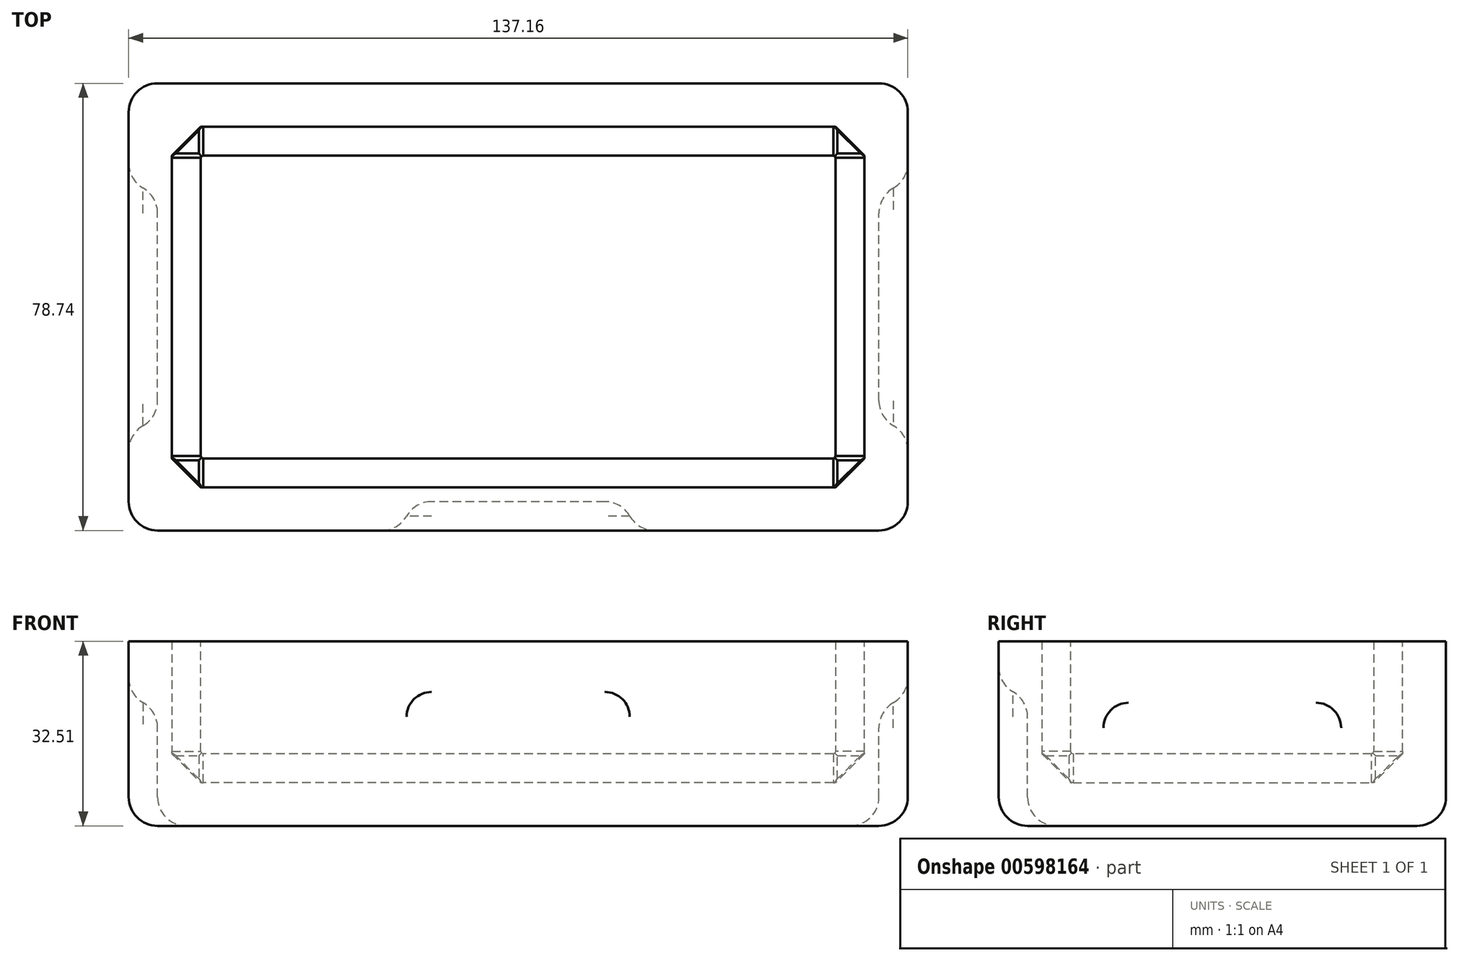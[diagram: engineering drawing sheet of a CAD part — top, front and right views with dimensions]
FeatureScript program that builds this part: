
annotation { "Feature Type Name" : "Feature", "Feature Type Description" : "" }
export const myFeature = defineFeature(function(context is Context, id is Id, definition is map)
    precondition{}
    {
        {
            var Q0;
            Q0=qCreatedBy(makeId("Top.planeOp"),FACE);
            var sketch = newSketch(context, id + "F0", { "sketchPlane" : qUnion([Q0])});
            skLineSegment(sketch, "E0.bottom", {"start": v(68.58, -39.37) * mm, "end": v(-68.58, -39.37) * mm});
            skLineSegment(sketch, "E0.top", {"start": v(68.58, 39.37) * mm, "end": v(-68.58, 39.37) * mm});
            skLineSegment(sketch, "E0.left", {"start": v(68.58, -39.37) * mm, "end": v(68.58, 39.37) * mm});
            skLineSegment(sketch, "E0.right", {"start": v(-68.58, -39.37) * mm, "end": v(-68.58, 39.37) * mm});
            skPoint(sketch, "E0.middle", {"position": v(0, 0) * mm});
            skSolve(sketch);
        }
        {
            var Q0;
            Q0 = qSketchRegion(id + "F0", true);
            extrude(context, id + "F1", {"entities" : qUnion([Q0]), "depth" : 32.5 * mm, "offsetDistance" : 25.4 * mm});
        }
        {
            var Q0;
            Q0=makeQuery(id+"F1.opExtrude","CAP_FACE",FACE,{"disambiguationData":[OSD([sQuery(id+"F0.wireOp",EDGE,"E0.bottom"),sQuery(id+"F0.wireOp",EDGE,"E0.top"),sQuery(id+"F0.wireOp",EDGE,"E0.left"),sQuery(id+"F0.wireOp",EDGE,"E0.right")])],"isStart":false});
            shell(context, id + "F2", {"entities" : qUnion([Q0]), "thickness" : 7.62 * mm});
        }
        {
            var Q0;
            Q0=makeQuery(id+"F2.opShell","OFFSET_EDGE",EDGE,{"disambiguationData":[OSD([sQuery(id+"F0.wireOp",EDGE,"E0.top"),sQuery(id+"F0.wireOp",EDGE,"E0.left")])]});
            var Q1;
            {var subQ0=sQuery(id+"F0.wireOp",EDGE,"E0.left");Q1=makeQuery(id+"F2.opShell","OFFSET_EDGE",EDGE,{"disambiguationData":[OSD([subQ0]),TDD([makeQuery(id+"F1.opExtrude","CAP_EDGE",EDGE,{"disambiguationData":[OSD([subQ0])],"isStart":true})])]});}
            var Q2;
            {var subQ0=sQuery(id+"F0.wireOp",EDGE,"E0.top");Q2=makeQuery(id+"F2.opShell","OFFSET_EDGE",EDGE,{"disambiguationData":[OSD([subQ0]),TDD([makeQuery(id+"F1.opExtrude","CAP_EDGE",EDGE,{"disambiguationData":[OSD([subQ0])],"isStart":true})])]});}
            var Q3;
            Q3=makeQuery(id+"F2.opShell","OFFSET_EDGE",EDGE,{"disambiguationData":[OSD([sQuery(id+"F0.wireOp",EDGE,"E0.top"),sQuery(id+"F0.wireOp",EDGE,"E0.right")])]});
            var Q4;
            {var subQ0=sQuery(id+"F0.wireOp",EDGE,"E0.right");Q4=makeQuery(id+"F2.opShell","OFFSET_EDGE",EDGE,{"disambiguationData":[OSD([subQ0]),TDD([makeQuery(id+"F1.opExtrude","CAP_EDGE",EDGE,{"disambiguationData":[OSD([subQ0])],"isStart":true})])]});}
            var Q5;
            {var subQ0=sQuery(id+"F0.wireOp",EDGE,"E0.bottom");Q5=makeQuery(id+"F2.opShell","OFFSET_EDGE",EDGE,{"disambiguationData":[OSD([subQ0]),TDD([makeQuery(id+"F1.opExtrude","CAP_EDGE",EDGE,{"disambiguationData":[OSD([subQ0])],"isStart":true})])]});}
            var Q6;
            Q6=makeQuery(id+"F2.opShell","OFFSET_EDGE",EDGE,{"disambiguationData":[OSD([sQuery(id+"F0.wireOp",EDGE,"E0.bottom"),sQuery(id+"F0.wireOp",EDGE,"E0.left")])]});
            var Q7;
            Q7=makeQuery(id+"F2.opShell","OFFSET_EDGE",EDGE,{"disambiguationData":[OSD([sQuery(id+"F0.wireOp",EDGE,"E0.bottom"),sQuery(id+"F0.wireOp",EDGE,"E0.right")])]});
            chamfer(context, id + "F3", {"entities" : qUnion([Q0, Q1, Q2, Q3, Q4, Q5, Q6, Q7]), "width" : 5.08 * mm, "tangentPropagation" : true});
        }
        {
            var Q0;
            Q0=makeQuery(id+"F1.opExtrude","SWEPT_FACE",FACE,{"disambiguationData":[OSD([sQuery(id+"F0.wireOp",EDGE,"E0.bottom")])]});
            var sketch = newSketch(context, id + "F4", { "sketchPlane" : qUnion([Q0])});
            skLineSegment(sketch, "E1.bottom", {"start": v(-20.32, 0) * mm, "end": v(20.32, 0) * mm});
            skLineSegment(sketch, "E1.top", {"start": v(-20.32, 24.27) * mm, "end": v(20.32, 24.27) * mm});
            skLineSegment(sketch, "E1.left", {"start": v(-20.32, 0) * mm, "end": v(-20.32, 24.27) * mm});
            skLineSegment(sketch, "E1.right", {"start": v(20.32, 0) * mm, "end": v(20.32, 24.27) * mm});
            skSolve(sketch);
        }
        {
            var Q0;
            Q0 = qSketchRegion(id + "F4", true);
            extrude(context, id + "F5", {"entities" : qUnion([Q0]), "operationType" : NewBodyOperationType.REMOVE, "oppositeDirection" : true, "depth" : 5.08 * mm, "offsetDistance" : 25.4 * mm});
        }
        {
            var Q0;
            Q0=makeQuery(id+"F1.opExtrude","SWEPT_FACE",FACE,{"disambiguationData":[OSD([sQuery(id+"F0.wireOp",EDGE,"E0.left")])]});
            var sketch = newSketch(context, id + "F6", { "sketchPlane" : qUnion([Q0])});
            skLineSegment(sketch, "E2.bottom", {"start": v(-21.6, 0) * mm, "end": v(21.59, 0) * mm});
            skLineSegment(sketch, "E2.top", {"start": v(-21.6, 22.35) * mm, "end": v(21.59, 22.35) * mm});
            skLineSegment(sketch, "E2.left", {"start": v(-21.6, 0) * mm, "end": v(-21.6, 22.35) * mm});
            skLineSegment(sketch, "E2.right", {"start": v(21.59, 0) * mm, "end": v(21.59, 22.35) * mm});
            skSolve(sketch);
        }
        {
            var Q0;
            Q0=makeQuery(id+"F6.imprint","IMPRINT",FACE,{"disambiguationData":[TD([[makeQuery(id+"F6.imprint","IMPRINT",EDGE,{"derivedFrom":sQuery(id+"F6.wireOp",EDGE,"E2.bottom")}),1.0]])]});
            extrude(context, id + "F7", {"entities" : qUnion([Q0]), "operationType" : NewBodyOperationType.REMOVE, "oppositeDirection" : true, "depth" : 5.08 * mm, "offsetDistance" : 25.4 * mm});
        }
        {
            var Q0;
            Q0=makeQuery(id+"F1.opExtrude","SWEPT_FACE",FACE,{"disambiguationData":[OSD([sQuery(id+"F0.wireOp",EDGE,"E0.right")])]});
            var sketch = newSketch(context, id + "F8", { "sketchPlane" : qUnion([Q0])});
            skLineSegment(sketch, "E3.bottom", {"start": v(-21.6, 0) * mm, "end": v(21.59, 0) * mm});
            skLineSegment(sketch, "E3.top", {"start": v(-21.6, 22.35) * mm, "end": v(21.59, 22.35) * mm});
            skLineSegment(sketch, "E3.left", {"start": v(-21.6, 0) * mm, "end": v(-21.6, 22.35) * mm});
            skLineSegment(sketch, "E3.right", {"start": v(21.59, 0) * mm, "end": v(21.59, 22.35) * mm});
            skSolve(sketch);
        }
        {
            var Q0;
            Q0 = qSketchRegion(id + "F8", true);
            extrude(context, id + "F9", {"entities" : qUnion([Q0]), "operationType" : NewBodyOperationType.REMOVE, "oppositeDirection" : true, "depth" : 5.08 * mm, "offsetDistance" : 25.4 * mm});
        }
        {
            var Q0;
            Q0=makeQuery(id+"F9.boolean.opBoolean","COPY",EDGE,{"derivedFrom":makeQuery(id+"F9.opExtrude","SWEPT_EDGE",EDGE,{"disambiguationData":[OSD([sQuery(id+"F8.wireOp",EDGE,"E3.top"),sQuery(id+"F8.wireOp",EDGE,"E3.left")])]})});
            var Q1;
            Q1=makeQuery(id+"F9.boolean.opBoolean","COPY",EDGE,{"derivedFrom":makeQuery(id+"F9.opExtrude","CAP_EDGE",EDGE,{"disambiguationData":[OSD([sQuery(id+"F8.wireOp",EDGE,"E3.top")])],"isStart":false})});
            var Q2;
            Q2=makeQuery(id+"F9.boolean.opBoolean","COPY",EDGE,{"derivedFrom":makeQuery(id+"F9.opExtrude","SWEPT_EDGE",EDGE,{"disambiguationData":[OSD([sQuery(id+"F8.wireOp",EDGE,"E3.top"),sQuery(id+"F8.wireOp",EDGE,"E3.right")])]})});
            var Q3;
            Q3=makeQuery(id+"F9.boolean.opBoolean","COPY",EDGE,{"derivedFrom":makeQuery(id+"F9.opExtrude","CAP_EDGE",EDGE,{"disambiguationData":[OSD([sQuery(id+"F8.wireOp",EDGE,"E3.left")])],"isStart":false})});
            var Q4;
            Q4=makeQuery(id+"F9.boolean.opBoolean","COPY",EDGE,{"derivedFrom":makeQuery(id+"F9.opExtrude","CAP_EDGE",EDGE,{"disambiguationData":[OSD([sQuery(id+"F8.wireOp",EDGE,"E3.right")])],"isStart":false})});
            fillet(context, id + "F10", {"entities" : qUnion([Q0, Q1, Q2, Q3, Q4]), "radius" : 5.08 * mm, "tangentPropagation" : true, "allowEdgeOverflow" : false});
        }
        {
            var Q0;
            Q0=makeQuery(id+"F5.boolean.opBoolean","COPY",EDGE,{"derivedFrom":makeQuery(id+"F5.opExtrude","SWEPT_EDGE",EDGE,{"disambiguationData":[OSD([sQuery(id+"F4.wireOp",EDGE,"E1.top"),sQuery(id+"F4.wireOp",EDGE,"E1.left")])]})});
            var Q1;
            Q1=makeQuery(id+"F5.boolean.opBoolean","COPY",EDGE,{"derivedFrom":makeQuery(id+"F5.opExtrude","CAP_EDGE",EDGE,{"disambiguationData":[OSD([sQuery(id+"F4.wireOp",EDGE,"E1.top")])],"isStart":false})});
            var Q2;
            Q2=makeQuery(id+"F5.boolean.opBoolean","COPY",EDGE,{"derivedFrom":makeQuery(id+"F5.opExtrude","SWEPT_EDGE",EDGE,{"disambiguationData":[OSD([sQuery(id+"F4.wireOp",EDGE,"E1.top"),sQuery(id+"F4.wireOp",EDGE,"E1.right")])]})});
            var Q3;
            Q3=makeQuery(id+"F5.boolean.opBoolean","COPY",EDGE,{"derivedFrom":makeQuery(id+"F5.opExtrude","CAP_EDGE",EDGE,{"disambiguationData":[OSD([sQuery(id+"F4.wireOp",EDGE,"E1.right")])],"isStart":false})});
            var Q4;
            Q4=makeQuery(id+"F5.boolean.opBoolean","COPY",EDGE,{"derivedFrom":makeQuery(id+"F5.opExtrude","CAP_EDGE",EDGE,{"disambiguationData":[OSD([sQuery(id+"F4.wireOp",EDGE,"E1.left")])],"isStart":false})});
            fillet(context, id + "F11", {"entities" : qUnion([Q0, Q1, Q2, Q3, Q4]), "radius" : 5.08 * mm, "tangentPropagation" : true, "allowEdgeOverflow" : false});
        }
        {
            var Q0;
            Q0=makeQuery(id+"F7.boolean.opBoolean","COPY",EDGE,{"derivedFrom":makeQuery(id+"F7.opExtrude","SWEPT_EDGE",EDGE,{"disambiguationData":[OSD([sQuery(id+"F6.wireOp",EDGE,"E2.top"),sQuery(id+"F6.wireOp",EDGE,"E2.left")])]})});
            var Q1;
            Q1=makeQuery(id+"F7.boolean.opBoolean","COPY",EDGE,{"derivedFrom":makeQuery(id+"F7.opExtrude","CAP_EDGE",EDGE,{"disambiguationData":[OSD([sQuery(id+"F6.wireOp",EDGE,"E2.top")])],"isStart":false})});
            var Q2;
            Q2=makeQuery(id+"F7.boolean.opBoolean","COPY",EDGE,{"derivedFrom":makeQuery(id+"F7.opExtrude","SWEPT_EDGE",EDGE,{"disambiguationData":[OSD([sQuery(id+"F6.wireOp",EDGE,"E2.top"),sQuery(id+"F6.wireOp",EDGE,"E2.right")])]})});
            var Q3;
            Q3=makeQuery(id+"F7.boolean.opBoolean","COPY",EDGE,{"derivedFrom":makeQuery(id+"F7.opExtrude","CAP_EDGE",EDGE,{"disambiguationData":[OSD([sQuery(id+"F6.wireOp",EDGE,"E2.right")])],"isStart":false})});
            var Q4;
            Q4=makeQuery(id+"F7.boolean.opBoolean","COPY",EDGE,{"derivedFrom":makeQuery(id+"F7.opExtrude","CAP_EDGE",EDGE,{"disambiguationData":[OSD([sQuery(id+"F6.wireOp",EDGE,"E2.left")])],"isStart":false})});
            fillet(context, id + "F12", {"entities" : qUnion([Q0, Q1, Q2, Q3, Q4]), "radius" : 5.08 * mm, "tangentPropagation" : true, "allowEdgeOverflow" : false});
        }
        {
            var Q0;
            Q0=makeQuery(id+"F12.opFillet","BLEND_EDGE",EDGE,{"blendedFrom":[makeQuery(id+"F7.boolean.opBoolean","COPY",EDGE,{"derivedFrom":makeQuery(id+"F7.opExtrude","CAP_EDGE",EDGE,{"disambiguationData":[OSD([sQuery(id+"F6.wireOp",EDGE,"E2.left")])],"isStart":false})}),makeQuery(id+"F1.opExtrude","SWEPT_FACE",FACE,{"disambiguationData":[OSD([sQuery(id+"F0.wireOp",EDGE,"E0.left")])]})],"blendedInto":[makeQuery(id+"F1.opExtrude","SWEPT_FACE",FACE,{"disambiguationData":[OSD([sQuery(id+"F0.wireOp",EDGE,"E0.left")])]})]});
            fillet(context, id + "F13", {"entities" : qUnion([Q0]), "radius" : 5.08 * mm, "tangentPropagation" : true, "allowEdgeOverflow" : false});
        }
        {
            var Q0;
            Q0=makeQuery(id+"F11.opFillet","BLEND_EDGE",EDGE,{"blendedFrom":[makeQuery(id+"F5.boolean.opBoolean","COPY",EDGE,{"derivedFrom":makeQuery(id+"F5.opExtrude","CAP_EDGE",EDGE,{"disambiguationData":[OSD([sQuery(id+"F4.wireOp",EDGE,"E1.left")])],"isStart":false})}),makeQuery(id+"F1.opExtrude","SWEPT_FACE",FACE,{"disambiguationData":[OSD([sQuery(id+"F0.wireOp",EDGE,"E0.bottom")])]})],"blendedInto":[makeQuery(id+"F1.opExtrude","SWEPT_FACE",FACE,{"disambiguationData":[OSD([sQuery(id+"F0.wireOp",EDGE,"E0.bottom")])]})]});
            fillet(context, id + "F14", {"entities" : qUnion([Q0]), "radius" : 5.08 * mm, "tangentPropagation" : true, "allowEdgeOverflow" : false});
        }
        {
            var Q0;
            Q0=makeQuery(id+"F10.opFillet","BLEND_EDGE",EDGE,{"blendedFrom":[makeQuery(id+"F9.boolean.opBoolean","COPY",EDGE,{"derivedFrom":makeQuery(id+"F9.opExtrude","CAP_EDGE",EDGE,{"disambiguationData":[OSD([sQuery(id+"F8.wireOp",EDGE,"E3.left")])],"isStart":false})}),makeQuery(id+"F1.opExtrude","SWEPT_FACE",FACE,{"disambiguationData":[OSD([sQuery(id+"F0.wireOp",EDGE,"E0.right")])]})],"blendedInto":[makeQuery(id+"F1.opExtrude","SWEPT_FACE",FACE,{"disambiguationData":[OSD([sQuery(id+"F0.wireOp",EDGE,"E0.right")])]})]});
            fillet(context, id + "F15", {"entities" : qUnion([Q0]), "radius" : 5.08 * mm, "tangentPropagation" : true, "allowEdgeOverflow" : false});
        }
        {
            var Q0;
            {var subQ0=sQuery(id+"F0.wireOp",EDGE,"E0.bottom");var subQ1=sQuery(id+"F0.wireOp",EDGE,"E0.left");Q0=makeQuery(id+"F5.boolean.opBoolean","SPLIT",EDGE,{"disambiguationData":[TD([makeQuery(id+"F1.opExtrude","SWEPT_FACE",FACE,{"disambiguationData":[OSD([subQ1])]})])],"derivedFrom":makeQuery(id+"F1.opExtrude","CAP_EDGE",EDGE,{"disambiguationData":[OSD([subQ0])],"isStart":true})});}
            var Q1;
            {var subQ0=sQuery(id+"F0.wireOp",EDGE,"E0.bottom");var subQ1=sQuery(id+"F0.wireOp",EDGE,"E0.left");Q1=makeQuery(id+"F7.boolean.opBoolean","SPLIT",EDGE,{"disambiguationData":[TD([makeQuery(id+"F1.opExtrude","SWEPT_FACE",FACE,{"disambiguationData":[OSD([subQ0])]})])],"derivedFrom":makeQuery(id+"F1.opExtrude","CAP_EDGE",EDGE,{"disambiguationData":[OSD([subQ1])],"isStart":true})});}
            var Q2;
            Q2=makeQuery(id+"F9.boolean.opBoolean","COPY",EDGE,{"derivedFrom":makeQuery(id+"F9.opExtrude","CAP_EDGE",EDGE,{"disambiguationData":[OSD([sQuery(id+"F8.wireOp",EDGE,"E3.bottom")])],"isStart":false})});
            var Q3;
            Q3=makeQuery(id+"F1.opExtrude","CAP_EDGE",EDGE,{"disambiguationData":[OSD([sQuery(id+"F0.wireOp",EDGE,"E0.top")])],"isStart":true});
            fillet(context, id + "F16", {"entities" : qUnion([Q0, Q1, Q2, Q3]), "radius" : 5.08 * mm, "tangentPropagation" : true, "allowEdgeOverflow" : false});
        }
        {
            var Q0;
            {var subQ0=sQuery(id+"F0.wireOp",EDGE,"E0.right");var subQ1=sQuery(id+"F0.wireOp",EDGE,"E0.top");Q0=makeQuery(id+"F3.opChamfer","BLEND_EDGE",EDGE,{"blendedFrom":[makeQuery(id+"F2.opShell","OFFSET_VERTEX",VERTEX,{"disambiguationData":[OSD([subQ1,subQ0]),TDD([makeQuery(id+"F1.opExtrude","CAP_VERTEX",VERTEX,{"disambiguationData":[OSD([subQ1,subQ0])],"isStart":true})])]}),makeQuery(id+"F2.opShell","OFFSET_EDGE",EDGE,{"disambiguationData":[OSD([subQ1,subQ0])]})],"blendedInto":[]});}
            var Q1;
            {var subQ0=sQuery(id+"F0.wireOp",EDGE,"E0.right");var subQ1=sQuery(id+"F0.wireOp",EDGE,"E0.top");Q1=makeQuery(id+"F3.opChamfer","BLEND_EDGE",EDGE,{"blendedFrom":[makeQuery(id+"F2.opShell","OFFSET_VERTEX",VERTEX,{"disambiguationData":[OSD([subQ1,subQ0]),TDD([makeQuery(id+"F1.opExtrude","CAP_VERTEX",VERTEX,{"disambiguationData":[OSD([subQ1,subQ0])],"isStart":true})])]}),makeQuery(id+"F2.opShell","OFFSET_EDGE",EDGE,{"disambiguationData":[OSD([subQ0]),TDD([makeQuery(id+"F1.opExtrude","CAP_EDGE",EDGE,{"disambiguationData":[OSD([subQ0])],"isStart":true})])]})],"blendedInto":[]});}
            var Q2;
            {var subQ0=sQuery(id+"F0.wireOp",EDGE,"E0.top");var subQ1=sQuery(id+"F0.wireOp",EDGE,"E0.right");Q2=makeQuery(id+"F3.opChamfer","BLEND_EDGE",EDGE,{"blendedFrom":[makeQuery(id+"F2.opShell","OFFSET_VERTEX",VERTEX,{"disambiguationData":[OSD([subQ0,subQ1]),TDD([makeQuery(id+"F1.opExtrude","CAP_VERTEX",VERTEX,{"disambiguationData":[OSD([subQ0,subQ1])],"isStart":true})])]}),makeQuery(id+"F2.opShell","OFFSET_EDGE",EDGE,{"disambiguationData":[OSD([subQ0]),TDD([makeQuery(id+"F1.opExtrude","CAP_EDGE",EDGE,{"disambiguationData":[OSD([subQ0])],"isStart":true})])]})],"blendedInto":[]});}
            var Q3;
            {var subQ0=sQuery(id+"F0.wireOp",EDGE,"E0.right");var subQ1=sQuery(id+"F0.wireOp",EDGE,"E0.bottom");Q3=makeQuery(id+"F3.opChamfer","BLEND_EDGE",EDGE,{"blendedFrom":[makeQuery(id+"F2.opShell","OFFSET_VERTEX",VERTEX,{"disambiguationData":[OSD([subQ1,subQ0]),TDD([makeQuery(id+"F1.opExtrude","CAP_VERTEX",VERTEX,{"disambiguationData":[OSD([subQ1,subQ0])],"isStart":true})])]}),makeQuery(id+"F2.opShell","OFFSET_EDGE",EDGE,{"disambiguationData":[OSD([subQ1,subQ0])]})],"blendedInto":[]});}
            var Q4;
            {var subQ0=sQuery(id+"F0.wireOp",EDGE,"E0.right");var subQ1=sQuery(id+"F0.wireOp",EDGE,"E0.bottom");Q4=makeQuery(id+"F3.opChamfer","BLEND_EDGE",EDGE,{"blendedFrom":[makeQuery(id+"F2.opShell","OFFSET_VERTEX",VERTEX,{"disambiguationData":[OSD([subQ1,subQ0]),TDD([makeQuery(id+"F1.opExtrude","CAP_VERTEX",VERTEX,{"disambiguationData":[OSD([subQ1,subQ0])],"isStart":true})])]}),makeQuery(id+"F2.opShell","OFFSET_EDGE",EDGE,{"disambiguationData":[OSD([subQ0]),TDD([makeQuery(id+"F1.opExtrude","CAP_EDGE",EDGE,{"disambiguationData":[OSD([subQ0])],"isStart":true})])]})],"blendedInto":[]});}
            var Q5;
            {var subQ0=sQuery(id+"F0.wireOp",EDGE,"E0.bottom");var subQ1=sQuery(id+"F0.wireOp",EDGE,"E0.right");Q5=makeQuery(id+"F3.opChamfer","BLEND_EDGE",EDGE,{"blendedFrom":[makeQuery(id+"F2.opShell","OFFSET_VERTEX",VERTEX,{"disambiguationData":[OSD([subQ0,subQ1]),TDD([makeQuery(id+"F1.opExtrude","CAP_VERTEX",VERTEX,{"disambiguationData":[OSD([subQ0,subQ1])],"isStart":true})])]}),makeQuery(id+"F2.opShell","OFFSET_EDGE",EDGE,{"disambiguationData":[OSD([subQ0]),TDD([makeQuery(id+"F1.opExtrude","CAP_EDGE",EDGE,{"disambiguationData":[OSD([subQ0])],"isStart":true})])]})],"blendedInto":[]});}
            var Q6;
            {var subQ0=sQuery(id+"F0.wireOp",EDGE,"E0.left");var subQ1=sQuery(id+"F0.wireOp",EDGE,"E0.top");Q6=makeQuery(id+"F3.opChamfer","BLEND_EDGE",EDGE,{"blendedFrom":[makeQuery(id+"F2.opShell","OFFSET_VERTEX",VERTEX,{"disambiguationData":[OSD([subQ1,subQ0]),TDD([makeQuery(id+"F1.opExtrude","CAP_VERTEX",VERTEX,{"disambiguationData":[OSD([subQ1,subQ0])],"isStart":true})])]}),makeQuery(id+"F2.opShell","OFFSET_EDGE",EDGE,{"disambiguationData":[OSD([subQ1,subQ0])]})],"blendedInto":[]});}
            var Q7;
            {var subQ0=sQuery(id+"F0.wireOp",EDGE,"E0.top");var subQ1=sQuery(id+"F0.wireOp",EDGE,"E0.left");Q7=makeQuery(id+"F3.opChamfer","BLEND_EDGE",EDGE,{"blendedFrom":[makeQuery(id+"F2.opShell","OFFSET_VERTEX",VERTEX,{"disambiguationData":[OSD([subQ0,subQ1]),TDD([makeQuery(id+"F1.opExtrude","CAP_VERTEX",VERTEX,{"disambiguationData":[OSD([subQ0,subQ1])],"isStart":true})])]}),makeQuery(id+"F2.opShell","OFFSET_EDGE",EDGE,{"disambiguationData":[OSD([subQ0]),TDD([makeQuery(id+"F1.opExtrude","CAP_EDGE",EDGE,{"disambiguationData":[OSD([subQ0])],"isStart":true})])]})],"blendedInto":[]});}
            var Q8;
            {var subQ0=sQuery(id+"F0.wireOp",EDGE,"E0.left");var subQ1=sQuery(id+"F0.wireOp",EDGE,"E0.top");Q8=makeQuery(id+"F3.opChamfer","BLEND_EDGE",EDGE,{"blendedFrom":[makeQuery(id+"F2.opShell","OFFSET_VERTEX",VERTEX,{"disambiguationData":[OSD([subQ1,subQ0]),TDD([makeQuery(id+"F1.opExtrude","CAP_VERTEX",VERTEX,{"disambiguationData":[OSD([subQ1,subQ0])],"isStart":true})])]}),makeQuery(id+"F2.opShell","OFFSET_EDGE",EDGE,{"disambiguationData":[OSD([subQ0]),TDD([makeQuery(id+"F1.opExtrude","CAP_EDGE",EDGE,{"disambiguationData":[OSD([subQ0])],"isStart":true})])]})],"blendedInto":[]});}
            var Q9;
            {var subQ0=sQuery(id+"F0.wireOp",EDGE,"E0.bottom");var subQ1=sQuery(id+"F0.wireOp",EDGE,"E0.left");Q9=makeQuery(id+"F3.opChamfer","BLEND_EDGE",EDGE,{"blendedFrom":[makeQuery(id+"F2.opShell","OFFSET_VERTEX",VERTEX,{"disambiguationData":[OSD([subQ0,subQ1]),TDD([makeQuery(id+"F1.opExtrude","CAP_VERTEX",VERTEX,{"disambiguationData":[OSD([subQ0,subQ1])],"isStart":true})])]}),makeQuery(id+"F2.opShell","OFFSET_EDGE",EDGE,{"disambiguationData":[OSD([subQ0]),TDD([makeQuery(id+"F1.opExtrude","CAP_EDGE",EDGE,{"disambiguationData":[OSD([subQ0])],"isStart":true})])]})],"blendedInto":[]});}
            var Q10;
            {var subQ0=sQuery(id+"F0.wireOp",EDGE,"E0.left");var subQ1=sQuery(id+"F0.wireOp",EDGE,"E0.bottom");Q10=makeQuery(id+"F3.opChamfer","BLEND_EDGE",EDGE,{"blendedFrom":[makeQuery(id+"F2.opShell","OFFSET_VERTEX",VERTEX,{"disambiguationData":[OSD([subQ1,subQ0]),TDD([makeQuery(id+"F1.opExtrude","CAP_VERTEX",VERTEX,{"disambiguationData":[OSD([subQ1,subQ0])],"isStart":true})])]}),makeQuery(id+"F2.opShell","OFFSET_EDGE",EDGE,{"disambiguationData":[OSD([subQ0]),TDD([makeQuery(id+"F1.opExtrude","CAP_EDGE",EDGE,{"disambiguationData":[OSD([subQ0])],"isStart":true})])]})],"blendedInto":[]});}
            var Q11;
            {var subQ0=sQuery(id+"F0.wireOp",EDGE,"E0.left");var subQ1=sQuery(id+"F0.wireOp",EDGE,"E0.bottom");Q11=makeQuery(id+"F3.opChamfer","BLEND_EDGE",EDGE,{"blendedFrom":[makeQuery(id+"F2.opShell","OFFSET_VERTEX",VERTEX,{"disambiguationData":[OSD([subQ1,subQ0]),TDD([makeQuery(id+"F1.opExtrude","CAP_VERTEX",VERTEX,{"disambiguationData":[OSD([subQ1,subQ0])],"isStart":true})])]}),makeQuery(id+"F2.opShell","OFFSET_EDGE",EDGE,{"disambiguationData":[OSD([subQ1,subQ0])]})],"blendedInto":[]});}
            chamfer(context, id + "F17", {"entities" : qUnion([Q0, Q1, Q2, Q3, Q4, Q5, Q6, Q7, Q8, Q9, Q10, Q11]), "width" : 1.27 * mm, "tangentPropagation" : true});
        }
        {
            var Q0;
            Q0=makeQuery(id+"F1.opExtrude","SWEPT_EDGE",EDGE,{"disambiguationData":[OSD([sQuery(id+"F0.wireOp",EDGE,"E0.bottom"),sQuery(id+"F0.wireOp",EDGE,"E0.left")])]});
            var Q1;
            Q1=makeQuery(id+"F1.opExtrude","SWEPT_EDGE",EDGE,{"disambiguationData":[OSD([sQuery(id+"F0.wireOp",EDGE,"E0.top"),sQuery(id+"F0.wireOp",EDGE,"E0.left")])]});
            var Q2;
            Q2=makeQuery(id+"F1.opExtrude","SWEPT_EDGE",EDGE,{"disambiguationData":[OSD([sQuery(id+"F0.wireOp",EDGE,"E0.bottom"),sQuery(id+"F0.wireOp",EDGE,"E0.right")])]});
            var Q3;
            Q3=makeQuery(id+"F1.opExtrude","SWEPT_EDGE",EDGE,{"disambiguationData":[OSD([sQuery(id+"F0.wireOp",EDGE,"E0.top"),sQuery(id+"F0.wireOp",EDGE,"E0.right")])]});
            fillet(context, id + "F18", {"entities" : qUnion([Q0, Q1, Q2, Q3]), "radius" : 5.08 * mm, "tangentPropagation" : true, "allowEdgeOverflow" : false});
        }
    });
